# Revit family: Camera-Security-iPRO-2MP-PTZ-Network-U6530X_B6530XSeriesX
name_source: partatom
category: Security Devices
units: mm (PartAtom-declared; Revit-internal decimal feet)

## family parameters
Cut with Voids When Loaded = No
Host = Face
Maintain Annotation Orientation = No
OmniClass Number = 23.85.10.14.11
OmniClass Title = Cameras
Part Type = Normal
Room Calculation Point = No
Round Connector Dimension = Use Diameter
Shared = No

## types (4) — shared parameters
Alarm Input Or Output Specification = ALARM IN 1 (Alarm input 1/ Black & white input/ Auto time adjustment input) (x1), ALARM IN 2 (Alarm input 2/ ALARM OUT) (x1), ALARM IN 3 (Alarm input 3/ AUX OUT) (x1)
Audio In = Yes
Audio Out = Yes
Base Bracket Height = 1.417 "
Base Height = 2.205 "
Base Radius = 3.031 "
Communication Ports = 10Base-T / 100Base-TX, RJ45 connector
Date Last Modified = 2022/08/26
Day Or Night = Yes
Decoration Cover Height = 0.52 "
Decoration Cover Hole Radius = 1.634 "
Decoration Cover Radius = 4.14 "
Decoration Cover Wall Height = 0.118 "
Diameter = 6.496 "
Dome Bottom Offset = 0.197 "
Dome Diameter = 3.307 "
Equipment Abbreviation = SC
Family Version = 1.0.0
Full HD = Resolution : Full HD
HD = Resolution : HD
Has POE = Yes
IP Or Analog = IP
Indoor Or Outdoor = Outdoor
Manufacturer = i-PRO Co., Ltd.
Minimum Illumination = 0.015 lx
Model Disclaimer = Contact i-PRO for more information
Mounting Positions = Mount Dependent or Surface Mount
Operational Humidity = 10 to 100 % (no condensation)
Operational Temperature = -30 °C to +55 °C (-22 °F to +131 °F)
Pan Max = 360.00°
Pan Min = 0.00°
Panning Range = 0 to 360
Product Material = Paint - i-Pro White
Provide Feedback = https://i-pro.com
Regulatory Compliance = UL (UL62368-1), c-UL (CSA C22.2 No.62368-1), CE, IEC62368-1, FCC (Part15 ClassA), ICES-003 Issue 7 ClassA, EN55032 ClassA, EN55035
Shock Resistance = IK10 (IEC 62262)
Storage Temperature = -30 °C to +65 °C (-22 °F to +136°F)
Tilt Max = 195.00°
Tilt Min = -15.00°
Tilting Range = -15 to +195
URL = https://i-pro.com
Vandal Resistant = Yes
Water and Dust Resistance = IP66, IEC60529 measuring standard compatible, Type 4X(UL50E), NEMA 4X compliant
Wide Dynamic Range = Yes
z Const Pan Handle Length = 19.488 "
z Const Tilt Base Length = 9.843 "
z Const Tilt Base2 Length = 19.685 "
z Const Tilt Handle Length = 11.811 "
z Const Yaw Base Length = 10.236 "
z Const Yaw Base2 Length = 17.323 "
z Const Yaw Handle Length = 9.252 "
z Level Offset = 7.874 "
zero-valued in all types: Default Elevation

## per-type parameters (varying)
| type | Angle Of View | Description | HFOV Max 169 | HFOV Max 43 | HFOV Min 169 | HFOV Min 43 | Height | Part Description | Product Documentation Link | Product Page URL | VFOV Max 169 | VFOV Max 43 | VFOV Min 169 | VFOV Min 43 | z Camera Height | z Camera Type | z VV Viewpoint Depth Max | z VV Viewpoint Depth Min |
| WV-U65301-Z1 | 62 | Security Camera, 2MP 10x Outdoor PTZ Network Camera, WV-U65301-Z1 | 62.00° | 48.00° | 6.70° | 5.10° | 5.472 " | Security Camera, 2MP 10x Outdoor PTZ Network Camera, WV-U65301-Z1 | https://bizpartner.panasonic.net | https://i-pro.com | 37.00° | 37.00° | 3.80° | 3.80° | 5.748 " | 11 | 1.805 " | 1.805 " |
| WV-B65301-Z1 | 62 | Security Camera, 2MP 10x Outdoor PTZ Network Camera, WV-B65301-Z1 | 62.00° | 48.00° | 6.70° | 5.10° | 5.472 " | Security Camera, 2MP 10x Outdoor PTZ Network Camera, WV-B65301-Z1 | https://japancs.i-pro.com | https://cwc.i-pro.com | 37.00° | 37.00° | 3.80° | 3.80° | 5.748 " | 21 | 1.805 " | 1.805 " |
| WV-U65302-Z2 | 77 | Security Camera, 2MP 21x Outdoor PTZ Network Comera, WV-U65302-Z2 | 77.00° | 58.00° | 3.70° | 2.90° | 6.024 " | Security Camera, 2MP 21x Outdoor PTZ Network Comera, WV-U65302-Z2 | https://bizpartner.panasonic.net | https://i-pro.com | 44.00° | 44.00° | 2.20° | 2.20° | 6.299 " | 12 | 1.7 " | 1.7 " |
| WV-B65302-Z2 | 77 | Security Camera, 2MP 21x Outdoor PTZ Network Camera, WV-B65302-Z2 | 77.00° | 58.00° | 3.70° | 2.90° | 6.024 " | Security Camera, 2MP 21x Outdoor PTZ Network Camera, WV-B65302-Z2 | https://japancs.i-pro.com | https://cwc.i-pro.com | 44.00° | 44.00° | 2.20° | 2.20° | 6.299 " | 22 | 1.7 " | 1.7 " |

note: column(s) folded — value = type name in every type: Model, Part Number

## geometry (parser evidence)
native form markers: Blend x2, Sweep x9
no freeform markers — native parametric forms only
